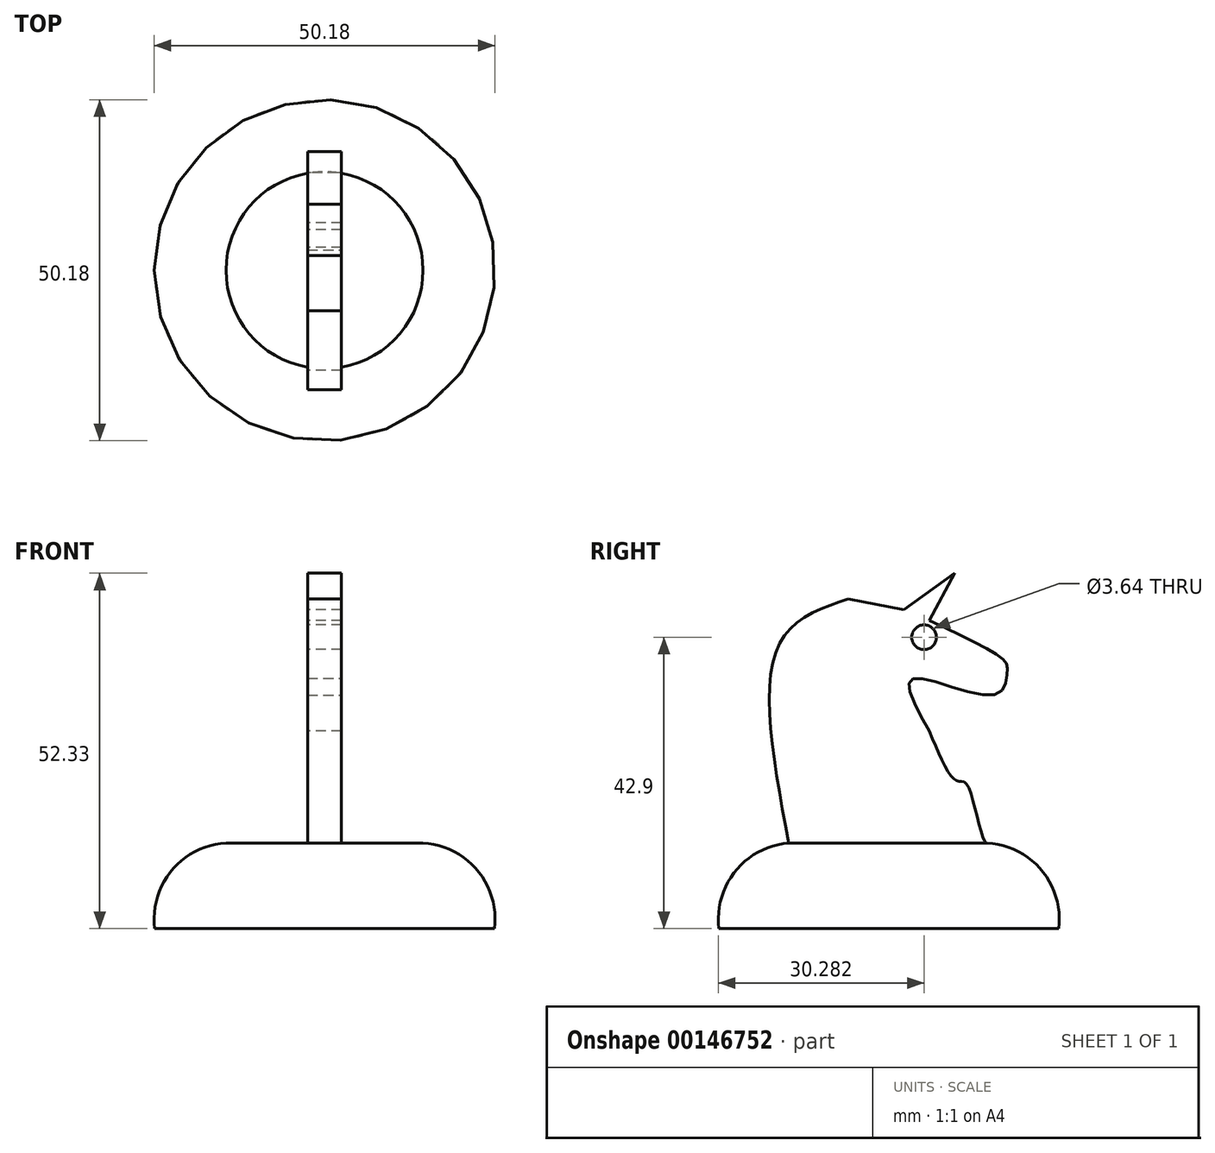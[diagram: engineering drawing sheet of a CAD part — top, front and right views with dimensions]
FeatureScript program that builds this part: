
annotation { "Feature Type Name" : "Feature", "Feature Type Description" : "" }
export const myFeature = defineFeature(function(context is Context, id is Id, definition is map)
    precondition{}
    {
        {
            var Q0;
            Q0=qCreatedBy(makeId("Front.planeOp"),FACE);
            var sketch = newSketch(context, id + "F0", { "sketchPlane" : qUnion([Q0])});
            skLineSegment(sketch, "E0", {"start": v(0, 0) * mm, "end": v(25, 0) * mm});
            skLineSegment(sketch, "E1.MirrorCS", {"start": v(0, 0) * mm, "end": v(-25, 0) * mm});
            skLineSegment(sketch, "E2", {"start": v(0, 0) * mm, "end": v(0, 12.81) * mm});
            skArc(sketch, "E3", {"start": v(25, 0) * mm, "mid": v(22.5, 8.6) * mm, "end": v(14.5, 12.61) * mm});
            skArc(sketch, "E4.MirrorCS", {"start": v(-25, 0) * mm, "mid": v(-22.5, 8.6) * mm, "end": v(-14.5, 12.61) * mm});
            skLineSegment(sketch, "E5", {"start": v(14.5, 12.61) * mm, "end": v(-14.5, 12.61) * mm});
            skSolve(sketch);
        }
        {
            var Q0;
            Q0=makeQuery(id+"F0.imprint","IMPRINT",FACE,{"disambiguationData":[TD([[makeQuery(id+"F0.imprint","IMPRINT",EDGE,{"derivedFrom":sQuery(id+"F0.wireOp",EDGE,"E0")}),1.0]])]});
            var Q1;
            Q1=sQuery(id+"F0.wireOp",EDGE,"E2");
            revolve(context, id + "F1", {"entities" : qUnion([Q0]), "axis" : qUnion([Q1]), "revolveType" : RevolveType.FULL});
        }
        {
            var Q0;
            Q0=qCreatedBy(makeId("Right.planeOp"),FACE);
            var sketch = newSketch(context, id + "F2", { "sketchPlane" : qUnion([Q0])});
            skLineSegment(sketch, "E6", {"start": v(-5.96, 48.56) * mm, "end": v(2.18, 46.97) * mm});
            skLineSegment(sketch, "E7", {"start": v(2.18, 46.97) * mm, "end": v(9.73, 52.33) * mm});
            skLineSegment(sketch, "E8", {"start": v(9.73, 52.33) * mm, "end": v(5.96, 45.38) * mm});
            skFitSpline(sketch, "E9", {"points": [v(5.96, 45.38) * mm, v(16.94, 39.54) * mm, v(17.43, 37.95) * mm, v(15.75, 34.48) * mm, v(3.53, 36.76) * mm, v(5.96, 29.12) * mm], "startDerivative": vector(53.9, -25.1) * mm, "endDerivative": vector(27.79, -49.15) * mm});
            skFitSpline(sketch, "E10", {"points": [v(5.96, 29.12) * mm, v(9.99, 21.77) * mm, v(11.38, 21.37) * mm, v(14.16, 12.83) * mm, v(14.55, 12.51) * mm, v(14.36, 12.51) * mm], "startDerivative": vector(12.09, -29.29) * mm, "endDerivative": vector(-5.27, 0.1) * mm});
            skLineSegment(sketch, "E11", {"start": v(14.55, 12.51) * mm, "end": v(-14.73, 12.51) * mm});
            skFitSpline(sketch, "E12", {"points": [v(-5.96, 48.56) * mm, v(-16.09, 42) * mm, v(-14.73, 12.51) * mm], "startDerivative": vector(-31.47, -10.66) * mm, "endDerivative": vector(10.82, -57.97) * mm});
            skSolve(sketch);
        }
        {
            var Q0;
            Q0=makeQuery(id+"F2.imprint","IMPRINT",FACE,{"disambiguationData":[TD([[makeQuery(id+"F2.imprint","IMPRINT",EDGE,{"derivedFrom":sQuery(id+"F2.wireOp",EDGE,"E6")}),-1.0]])]});
            extrude(context, id + "F3", {"entities" : qUnion([Q0]), "operationType" : NewBodyOperationType.ADD, "endBound" : BoundingType.SYMMETRIC, "depth" : 5 * mm});
        }
        {
            var Q0;
            Q0=makeQuery(id+"F3.opExtrude","CAP_FACE",FACE,{"disambiguationData":[OSD([sQuery(id+"F2.wireOp",EDGE,"ewwOclgY-0H0G-XBYP-dfVQ-jouC9pT5QdZx"),sQuery(id+"F2.wireOp",EDGE,"CZKMW3KF-eYRq-MXls-DdER-TS31ygk0F0WE"),sQuery(id+"F2.wireOp",EDGE,"RoTj8U1b-WUJB-KEsy-jwFo-amj9rYAu6Huc"),sQuery(id+"F2.wireOp",EDGE,"ECO86PAB-YGui-PldG-5hRX-W9z8cKTmAZ5L"),sQuery(id+"F2.wireOp",EDGE,"EO5HI7gf-4eBT-BLIy-mCkU-7LWnqwp0452t"),sQuery(id+"F2.wireOp",EDGE,"E6"),sQuery(id+"F2.wireOp",EDGE,"E7"),sQuery(id+"F2.wireOp",EDGE,"E8"),sQuery(id+"F2.wireOp",EDGE,"E9"),sQuery(id+"F2.wireOp",EDGE,"E10"),sQuery(id+"F2.wireOp",EDGE,"E11")])],"isStart":true});
            var sketch = newSketch(context, id + "F4", { "sketchPlane" : qUnion([Q0])});
            skCircle(sketch, "E13", {"center": v(-5.2, 42.9) * mm, "radius": 1.82 * mm});
            skSolve(sketch);
        }
        {
            var Q0;
            Q0 = qSketchRegion(id + "F4", true);
            extrude(context, id + "F5", {"entities" : qUnion([Q0]), "operationType" : NewBodyOperationType.REMOVE, "endBound" : BoundingType.SYMMETRIC, "oppositeDirection" : true, "depth" : 25 * mm});
        }
    });
